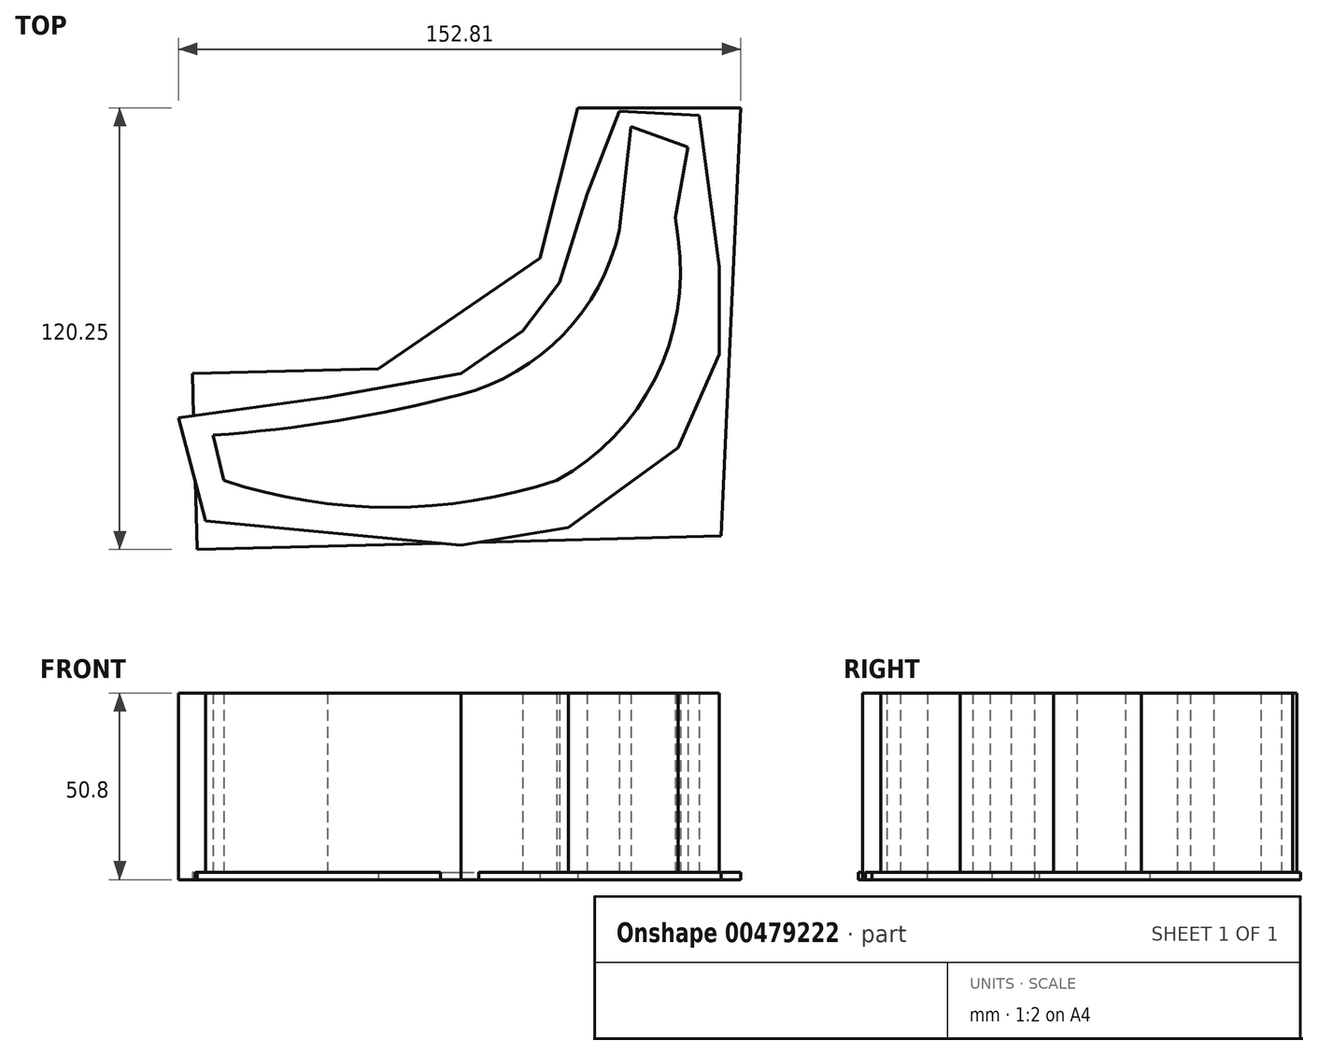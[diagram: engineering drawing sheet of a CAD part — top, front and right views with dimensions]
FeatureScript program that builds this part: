
annotation { "Feature Type Name" : "Feature", "Feature Type Description" : "" }
export const myFeature = defineFeature(function(context is Context, id is Id, definition is map)
    precondition{}
    {
        {
            var Q0;
            Q0=qCreatedBy(makeId("Top.planeOp"),FACE);
            var sketch = newSketch(context, id + "F0", { "sketchPlane" : qUnion([Q0])});
            skLineSegment(sketch, "E0", {"start": v(-67.46, -16.78) * mm, "end": v(-64.6, -29.08) * mm});
            skArc(sketch, "E1", {"start": v(-64.6, -29.08) * mm, "mid": v(-19.3, -36.42) * mm, "end": v(26, -29.08) * mm});
            skArc(sketch, "E2", {"start": v(26, -29.08) * mm, "mid": v(52.8, -1.34) * mm, "end": v(59.06, 36.7) * mm});
            skArc(sketch, "E3", {"start": v(0, -5.68) * mm, "mid": v(27.8, 10.57) * mm, "end": v(43.04, 38.94) * mm});
            skArc(sketch, "E4", {"start": v(-67.46, -16.78) * mm, "mid": v(-33.47, -12.81) * mm, "end": v(0, -5.68) * mm});
            skLineSegment(sketch, "E5", {"start": v(59.06, 36.7) * mm, "end": v(58.26, 42.4) * mm});
            skLineSegment(sketch, "E6", {"start": v(58.26, 42.4) * mm, "end": v(61.7, 61.67) * mm});
            skLineSegment(sketch, "E7", {"start": v(64.71, 70.2) * mm, "end": v(43.02, 71.33) * mm});
            skLineSegment(sketch, "E8", {"start": v(43.04, 38.94) * mm, "end": v(46.15, 67.2) * mm});
            skLineSegment(sketch, "E9", {"start": v(46.15, 67.2) * mm, "end": v(61.7, 61.67) * mm});
            skLineSegment(sketch, "E10", {"start": v(43.02, 71.33) * mm, "end": v(34.23, 48.8) * mm});
            skLineSegment(sketch, "E11", {"start": v(34.23, 48.8) * mm, "end": v(26.81, 24.78) * mm});
            skLineSegment(sketch, "E12", {"start": v(26.81, 24.78) * mm, "end": v(16.7, 11.6) * mm});
            skLineSegment(sketch, "E13", {"start": v(16.7, 11.6) * mm, "end": v(0, 0) * mm});
            skLineSegment(sketch, "E14", {"start": v(0, 0) * mm, "end": v(-36.33, -6.4) * mm});
            skLineSegment(sketch, "E15", {"start": v(-36.33, -6.4) * mm, "end": v(-76.79, -12.06) * mm});
            skLineSegment(sketch, "E16", {"start": v(0, -46.71) * mm, "end": v(29.23, -41.83) * mm});
            skLineSegment(sketch, "E17", {"start": v(29.23, -41.83) * mm, "end": v(59.1, -20.12) * mm});
            skLineSegment(sketch, "E18", {"start": v(59.1, -20.12) * mm, "end": v(70.22, 5.26) * mm});
            skLineSegment(sketch, "E19", {"start": v(70.22, 5.26) * mm, "end": v(70.22, 29.1) * mm});
            skLineSegment(sketch, "E20", {"start": v(70.22, 29.1) * mm, "end": v(64.71, 70.2) * mm});
            skLineSegment(sketch, "E21", {"start": v(-76.79, -12.06) * mm, "end": v(-69.42, -40.09) * mm});
            skLineSegment(sketch, "E22", {"start": v(-69.42, -40.09) * mm, "end": v(0, -46.71) * mm});
            skSolve(sketch);
        }
        {
            var Q0;
            Q0 = qSketchRegion(id + "F0", true);
            extrude(context, id + "F1", {"entities" : qUnion([Q0]), "depth" : 50.8 * mm});
        }
        {
            var Q0;
            Q0=qCreatedBy(makeId("Top.planeOp"),FACE);
            var sketch = newSketch(context, id + "F2", { "sketchPlane" : qUnion([Q0])});
            skLineSegment(sketch, "E23", {"start": v(31.7, 72.34) * mm, "end": v(76.02, 72.34) * mm});
            skLineSegment(sketch, "E24", {"start": v(76.02, 72.34) * mm, "end": v(70.75, -44.19) * mm});
            skLineSegment(sketch, "E25", {"start": v(70.75, -44.19) * mm, "end": v(-71.82, -47.9) * mm});
            skLineSegment(sketch, "E26", {"start": v(-71.82, -47.9) * mm, "end": v(-73.07, 0) * mm});
            skLineSegment(sketch, "E27", {"start": v(-73.07, 0) * mm, "end": v(-22.5, 1.32) * mm});
            skLineSegment(sketch, "E28", {"start": v(-22.5, 1.32) * mm, "end": v(21.47, 31.43) * mm});
            skLineSegment(sketch, "E29", {"start": v(21.47, 31.43) * mm, "end": v(31.7, 72.34) * mm});
            skSolve(sketch);
        }
        {
            var Q0;
            Q0 = qSketchRegion(id + "F2", true);
            extrude(context, id + "F3", {"entities" : qUnion([Q0]), "operationType" : NewBodyOperationType.ADD, "depth" : 2.03 * mm, "offsetDistance" : 25.4 * mm});
        }
    });
